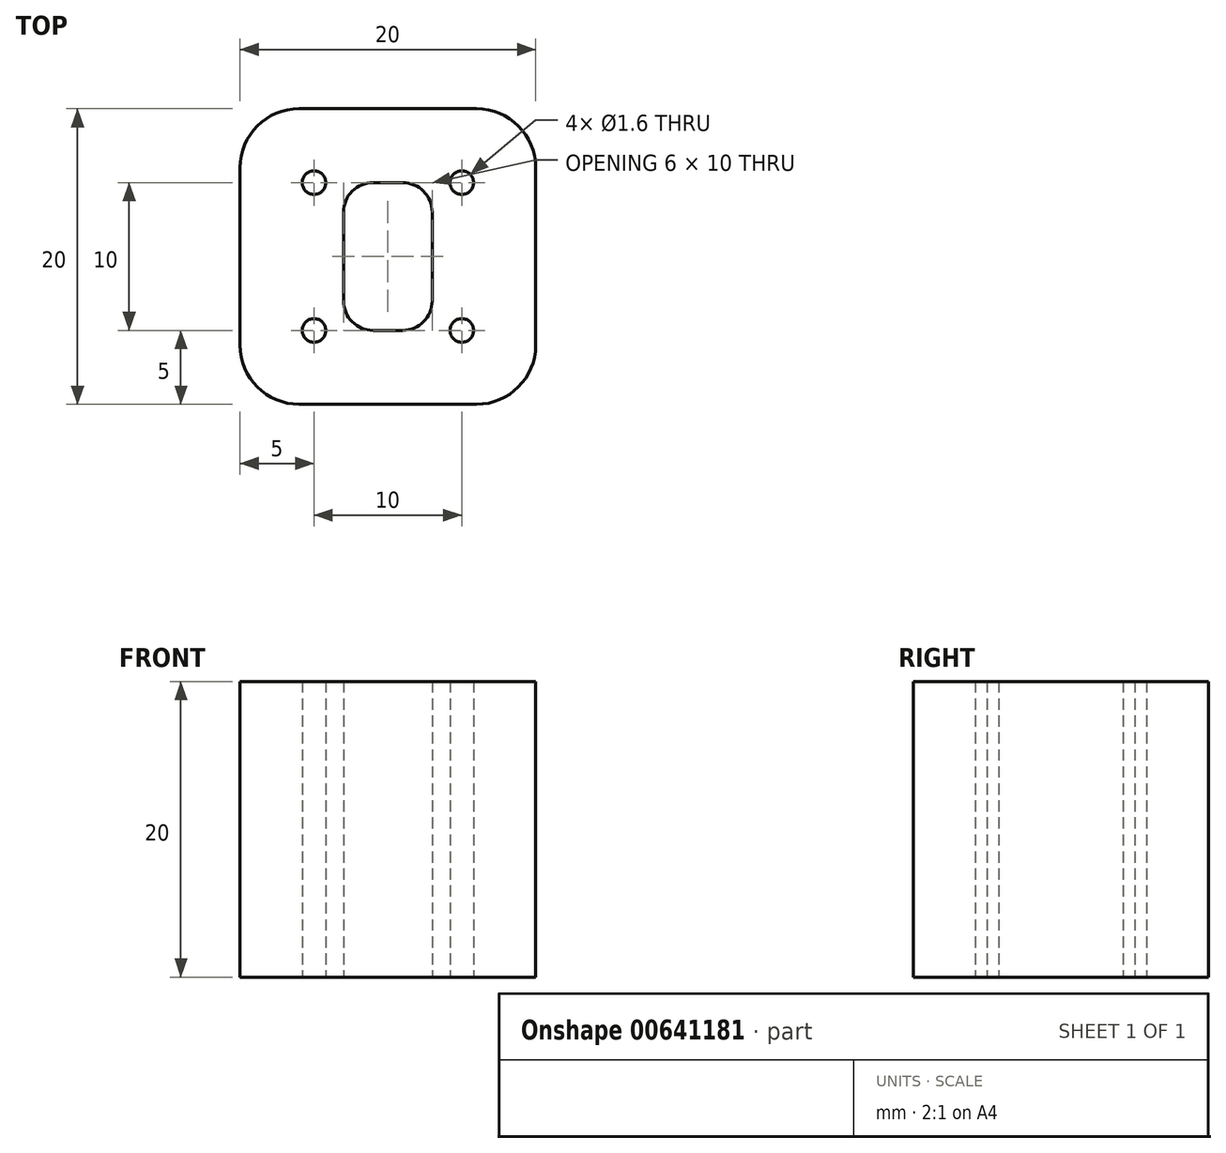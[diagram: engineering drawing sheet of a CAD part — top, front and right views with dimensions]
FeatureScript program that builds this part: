
annotation { "Feature Type Name" : "Feature", "Feature Type Description" : "" }
export const myFeature = defineFeature(function(context is Context, id is Id, definition is map)
    precondition{}
    {
        {
            var Q0;
            Q0=qCreatedBy(makeId("Top.planeOp"),FACE);
            var sketch = newSketch(context, id + "F0", { "sketchPlane" : qUnion([Q0])});
            skLineSegment(sketch, "E0", {"start": v(0, 5.56) * mm, "end": v(0, -5.09) * mm, "construction": true});
            skLineSegment(sketch, "E1", {"start": v(-3.98, 0) * mm, "end": v(3.95, 0) * mm, "construction": true});
            skCircle(sketch, "E2", {"center": v(-5, 5) * mm, "radius": 0.8 * mm});
            skCircle(sketch, "E3.MirrorC", {"center": v(5, 5) * mm, "radius": 0.8 * mm});
            skCircle(sketch, "E4.MirrorC", {"center": v(-5, -5) * mm, "radius": 0.8 * mm});
            skCircle(sketch, "E5.MirrorC", {"center": v(5, -5) * mm, "radius": 0.8 * mm});
            skLineSegment(sketch, "E6.bottom", {"start": v(-1, 5) * mm, "end": v(1, 5) * mm});
            skLineSegment(sketch, "E6.top", {"start": v(-1, -5) * mm, "end": v(1, -5) * mm});
            skLineSegment(sketch, "E6.left", {"start": v(-3, 3) * mm, "end": v(-3, -3) * mm});
            skLineSegment(sketch, "E6.right", {"start": v(3, 3) * mm, "end": v(3, -3) * mm});
            skPoint(sketch, "E7.visualSharp", {"position": v(-3, 5) * mm});
            skArc(sketch, "E7.filletArc", {"start": v(-1, 5) * mm, "mid": v(-2.41, 4.41) * mm, "end": v(-3, 3) * mm});
            skPoint(sketch, "E8.visualSharp", {"position": v(3, 5) * mm});
            skArc(sketch, "E8.filletArc", {"start": v(3, 3) * mm, "mid": v(2.41, 4.41) * mm, "end": v(1, 5) * mm});
            skPoint(sketch, "E9.visualSharp", {"position": v(3, -5) * mm});
            skArc(sketch, "E9.filletArc", {"start": v(1, -5) * mm, "mid": v(2.41, -4.41) * mm, "end": v(3, -3) * mm});
            skPoint(sketch, "E10.visualSharp", {"position": v(-3, -5) * mm});
            skArc(sketch, "E10.filletArc", {"start": v(-3, -3) * mm, "mid": v(-2.41, -4.41) * mm, "end": v(-1, -5) * mm});
            skLineSegment(sketch, "E11.bottom", {"start": v(-6, 10) * mm, "end": v(6, 10) * mm});
            skLineSegment(sketch, "E11.top", {"start": v(-6, -10) * mm, "end": v(6, -10) * mm});
            skLineSegment(sketch, "E11.left", {"start": v(-10, 6) * mm, "end": v(-10, -6) * mm});
            skLineSegment(sketch, "E11.right", {"start": v(10, 6) * mm, "end": v(10, -6) * mm});
            skPoint(sketch, "E12.visualSharp", {"position": v(-10, 10) * mm});
            skArc(sketch, "E12.filletArc", {"start": v(-6, 10) * mm, "mid": v(-8.83, 8.83) * mm, "end": v(-10, 6) * mm});
            skPoint(sketch, "E13.visualSharp", {"position": v(10, 10) * mm});
            skArc(sketch, "E13.filletArc", {"start": v(10, 6) * mm, "mid": v(8.83, 8.83) * mm, "end": v(6, 10) * mm});
            skPoint(sketch, "E14.visualSharp", {"position": v(10, -10) * mm});
            skArc(sketch, "E14.filletArc", {"start": v(6, -10) * mm, "mid": v(8.83, -8.83) * mm, "end": v(10, -6) * mm});
            skPoint(sketch, "E15.visualSharp", {"position": v(-10, -10) * mm});
            skArc(sketch, "E15.filletArc", {"start": v(-10, -6) * mm, "mid": v(-8.83, -8.83) * mm, "end": v(-6, -10) * mm});
            skSolve(sketch);
        }
        {
            var Q0;
            Q0=makeQuery(id+"F0.imprint","IMPRINT",FACE,{"disambiguationData":[TD([[makeQuery(id+"F0.imprint","IMPRINT",EDGE,{"derivedFrom":sQuery(id+"F0.wireOp",EDGE,"E2")}),-1.0]])]});
            extrude(context, id + "F1", {"entities" : qUnion([Q0]), "depth" : 20 * mm, "offsetDistance" : 25 * mm});
        }
    });
